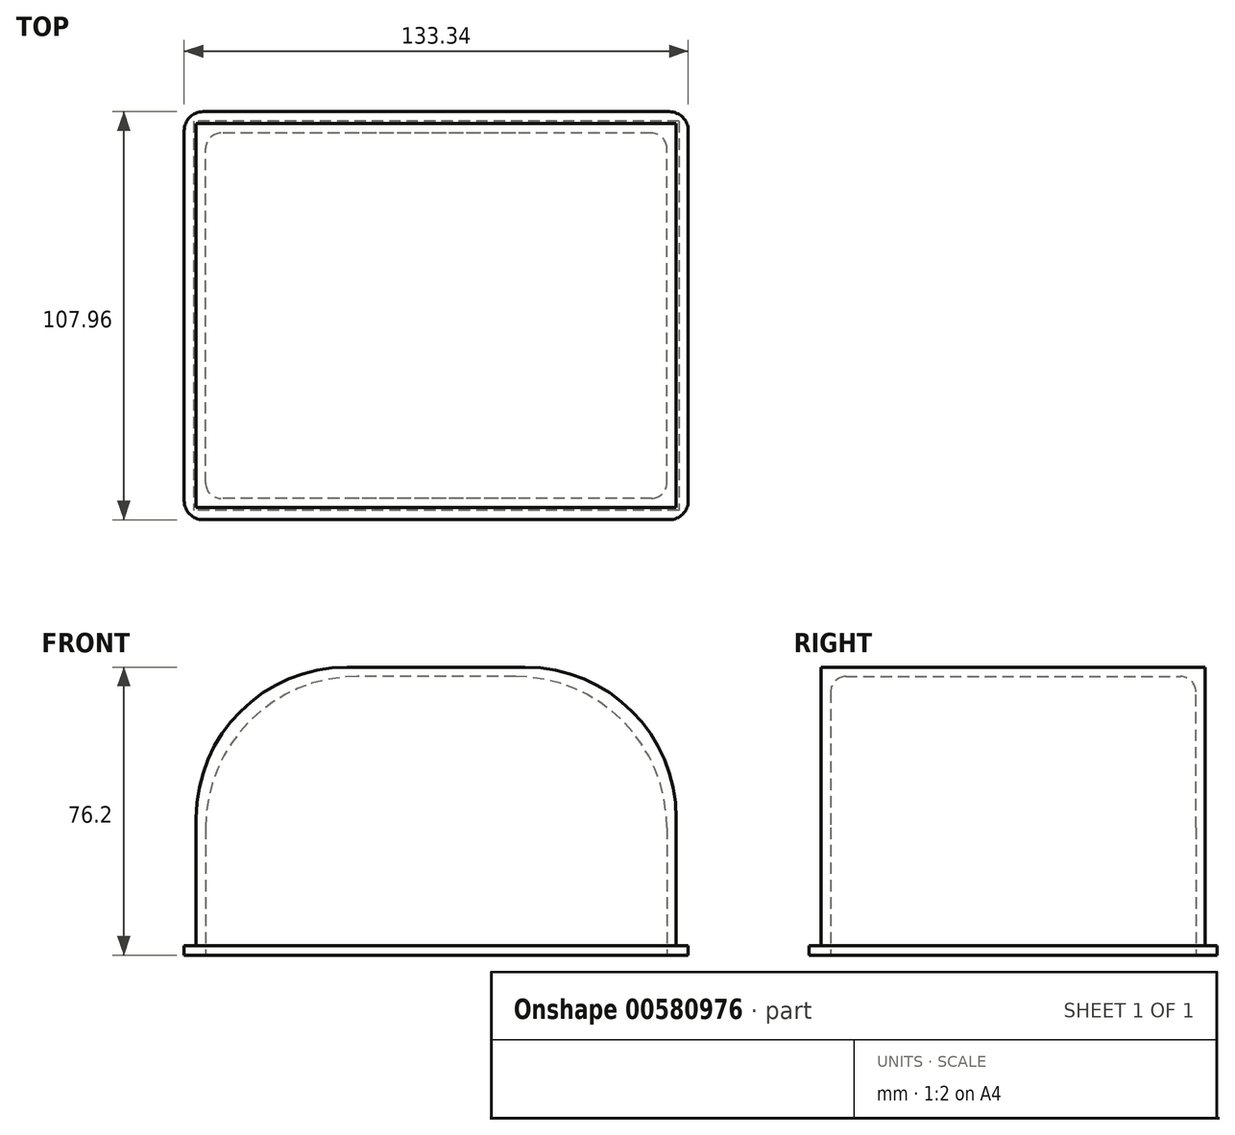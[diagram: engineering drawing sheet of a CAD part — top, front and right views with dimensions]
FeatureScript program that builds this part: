
annotation { "Feature Type Name" : "Feature", "Feature Type Description" : "" }
export const myFeature = defineFeature(function(context is Context, id is Id, definition is map)
    precondition{}
    {
        {
            var Q0;
            Q0=qCreatedBy(makeId("Top.planeOp"),FACE);
            var sketch = newSketch(context, id + "F0", { "sketchPlane" : qUnion([Q0])});
            skLineSegment(sketch, "E0.bottom", {"start": v(66.67, 53.98) * mm, "end": v(-66.68, 53.98) * mm});
            skLineSegment(sketch, "E0.top", {"start": v(66.68, -53.98) * mm, "end": v(-66.67, -53.98) * mm});
            skLineSegment(sketch, "E0.left", {"start": v(66.67, 53.98) * mm, "end": v(66.68, -53.98) * mm});
            skLineSegment(sketch, "E0.right", {"start": v(-66.68, 53.98) * mm, "end": v(-66.67, -53.98) * mm});
            skPoint(sketch, "E0.middle", {"position": v(0, 0) * mm});
            skSolve(sketch);
        }
        {
            var Q0;
            Q0=makeQuery(id+"F0.imprint","IMPRINT",FACE,{"disambiguationData":[TD([[makeQuery(id+"F0.imprint","IMPRINT",EDGE,{"derivedFrom":sQuery(id+"F0.wireOp",EDGE,"E0.bottom")}),1.0]])]});
            extrude(context, id + "F1", {"entities" : qUnion([Q0]), "depth" : 76.2 * mm, "offsetDistance" : 25 * mm});
        }
        {
            var Q0;
            Q0=qCreatedBy(makeId("Top.planeOp"),FACE);
            var sketch = newSketch(context, id + "F2", { "sketchPlane" : qUnion([Q0])});
            skLineSegment(sketch, "E1.bottom", {"start": v(63.5, -50.8) * mm, "end": v(-63.5, -50.8) * mm});
            skLineSegment(sketch, "E1.top", {"start": v(63.5, 50.8) * mm, "end": v(-63.5, 50.8) * mm});
            skLineSegment(sketch, "E1.left", {"start": v(63.5, -50.8) * mm, "end": v(63.5, 50.8) * mm});
            skLineSegment(sketch, "E1.right", {"start": v(-63.5, -50.8) * mm, "end": v(-63.5, 50.8) * mm});
            skPoint(sketch, "E1.middle", {"position": v(0, 0) * mm});
            skSolve(sketch);
        }
        {
            var Q0;
            Q0 = qSketchRegion(id + "F2", true);
            extrude(context, id + "F3", {"entities" : qUnion([Q0]), "operationType" : NewBodyOperationType.REMOVE, "depth" : 76.2 * mm, "offsetDistance" : 25 * mm});
        }
        {
            var Q0;
            Q0=makeQuery(id+"F1.opExtrude","CAP_FACE",FACE,{"disambiguationData":[OSD([sQuery(id+"F0.wireOp",EDGE,"E0.bottom"),sQuery(id+"F0.wireOp",EDGE,"E0.top"),sQuery(id+"F0.wireOp",EDGE,"E0.left"),sQuery(id+"F0.wireOp",EDGE,"E0.right")])],"isStart":false});
            extrude(context, id + "F4", {"entities" : qUnion([Q0]), "operationType" : NewBodyOperationType.REMOVE, "oppositeDirection" : true, "depth" : 73.66 * mm, "offsetDistance" : 25 * mm});
        }
        {
            var Q0;
            Q0=makeQuery(id+"F2.imprint","IMPRINT",FACE,{"disambiguationData":[TD([[makeQuery(id+"F2.imprint","IMPRINT",EDGE,{"derivedFrom":sQuery(id+"F2.wireOp",EDGE,"E1.bottom")}),-1.0]])]});
            extrude(context, id + "F5", {"entities" : qUnion([Q0]), "operationType" : NewBodyOperationType.ADD, "depth" : 76.2 * mm, "offsetDistance" : 25 * mm});
        }
        {
            var Q0;
            Q0=makeQuery(id+"F5.boolean.opBoolean","MERGE",FACE,{"derivedFrom":[makeQuery(id+"F1.opExtrude","CAP_FACE",FACE,{"disambiguationData":[OSD([sQuery(id+"F0.wireOp",EDGE,"E0.bottom"),sQuery(id+"F0.wireOp",EDGE,"E0.top"),sQuery(id+"F0.wireOp",EDGE,"E0.left"),sQuery(id+"F0.wireOp",EDGE,"E0.right")])],"isStart":true}),makeQuery(id+"F5.opExtrude","CAP_FACE",FACE,{"disambiguationData":[OSD([sQuery(id+"F2.wireOp",EDGE,"E1.bottom"),sQuery(id+"F2.wireOp",EDGE,"E1.top"),sQuery(id+"F2.wireOp",EDGE,"E1.left"),sQuery(id+"F2.wireOp",EDGE,"E1.right")])],"isStart":true})]});
            shell(context, id + "F6", {"entities" : qUnion([Q0]), "thickness" : 2.5 * mm});
        }
        {
            var Q0;
            {var subQ0=sQuery(id+"F2.wireOp",EDGE,"E1.right");Q0=makeQuery(id+"F6.opShell","OFFSET_EDGE",EDGE,{"disambiguationData":[OSD([subQ0]),TDD([makeQuery(id+"F5.opExtrude","CAP_EDGE",EDGE,{"disambiguationData":[OSD([subQ0])],"isStart":false})])]});}
            var Q1;
            {var subQ0=sQuery(id+"F2.wireOp",EDGE,"E1.left");Q1=makeQuery(id+"F6.opShell","OFFSET_EDGE",EDGE,{"disambiguationData":[OSD([subQ0]),TDD([makeQuery(id+"F5.opExtrude","CAP_EDGE",EDGE,{"disambiguationData":[OSD([subQ0])],"isStart":false})])]});}
            fillet(context, id + "F7", {"entities" : qUnion([Q0, Q1]), "radius" : 40 * mm, "tangentPropagation" : true, "allowEdgeOverflow" : false});
        }
        {
            var Q0;
            {var subQ0=sQuery(id+"F2.wireOp",EDGE,"E1.right");Q0=makeQuery(id+"F7.opFillet","BLEND_EDGE",EDGE,{"blendedFrom":[makeQuery(id+"F6.opShell","OFFSET_EDGE",EDGE,{"disambiguationData":[OSD([subQ0]),TDD([makeQuery(id+"F5.opExtrude","CAP_EDGE",EDGE,{"disambiguationData":[OSD([subQ0])],"isStart":false})])]}),makeQuery(id+"F6.opShell","OFFSET_FACE",FACE,{"disambiguationData":[OSD([sQuery(id+"F2.wireOp",EDGE,"E1.bottom")])]})],"blendedInto":[makeQuery(id+"F6.opShell","OFFSET_FACE",FACE,{"disambiguationData":[OSD([sQuery(id+"F2.wireOp",EDGE,"E1.bottom")])]})]});}
            var Q1;
            {var subQ0=sQuery(id+"F2.wireOp",EDGE,"E1.left");Q1=makeQuery(id+"F7.opFillet","BLEND_EDGE",EDGE,{"blendedFrom":[makeQuery(id+"F6.opShell","OFFSET_EDGE",EDGE,{"disambiguationData":[OSD([subQ0]),TDD([makeQuery(id+"F5.opExtrude","CAP_EDGE",EDGE,{"disambiguationData":[OSD([subQ0])],"isStart":false})])]}),makeQuery(id+"F6.opShell","OFFSET_FACE",FACE,{"disambiguationData":[OSD([sQuery(id+"F2.wireOp",EDGE,"E1.top")])]})],"blendedInto":[makeQuery(id+"F6.opShell","OFFSET_FACE",FACE,{"disambiguationData":[OSD([sQuery(id+"F2.wireOp",EDGE,"E1.top")])]})]});}
            fillet(context, id + "F8", {"entities" : qUnion([Q0, Q1]), "radius" : 4 * mm, "tangentPropagation" : true, "allowEdgeOverflow" : false});
        }
        {
            var Q0;
            Q0=makeQuery(id+"F1.opExtrude","SWEPT_EDGE",EDGE,{"disambiguationData":[OSD([sQuery(id+"F0.wireOp",EDGE,"E0.bottom"),sQuery(id+"F0.wireOp",EDGE,"E0.left")])]});
            var Q1;
            Q1=makeQuery(id+"F1.opExtrude","SWEPT_EDGE",EDGE,{"disambiguationData":[OSD([sQuery(id+"F0.wireOp",EDGE,"E0.top"),sQuery(id+"F0.wireOp",EDGE,"E0.left")])]});
            var Q2;
            Q2=makeQuery(id+"F1.opExtrude","SWEPT_EDGE",EDGE,{"disambiguationData":[OSD([sQuery(id+"F0.wireOp",EDGE,"E0.top"),sQuery(id+"F0.wireOp",EDGE,"E0.right")])]});
            var Q3;
            Q3=makeQuery(id+"F1.opExtrude","SWEPT_EDGE",EDGE,{"disambiguationData":[OSD([sQuery(id+"F0.wireOp",EDGE,"E0.bottom"),sQuery(id+"F0.wireOp",EDGE,"E0.right")])]});
            fillet(context, id + "F9", {"entities" : qUnion([Q0, Q1, Q2, Q3]), "radius" : 5 * mm, "tangentPropagation" : true, "allowEdgeOverflow" : false});
        }
        {
            var Q0;
            Q0=makeQuery(id+"F5.opExtrude","CAP_EDGE",EDGE,{"disambiguationData":[OSD([sQuery(id+"F2.wireOp",EDGE,"E1.right")])],"isStart":false});
            var Q1;
            Q1=makeQuery(id+"F5.opExtrude","CAP_EDGE",EDGE,{"disambiguationData":[OSD([sQuery(id+"F2.wireOp",EDGE,"E1.left")])],"isStart":false});
            fillet(context, id + "F10", {"entities" : qUnion([Q0, Q1]), "radius" : 40 * mm, "tangentPropagation" : true, "allowEdgeOverflow" : false});
        }
    });
